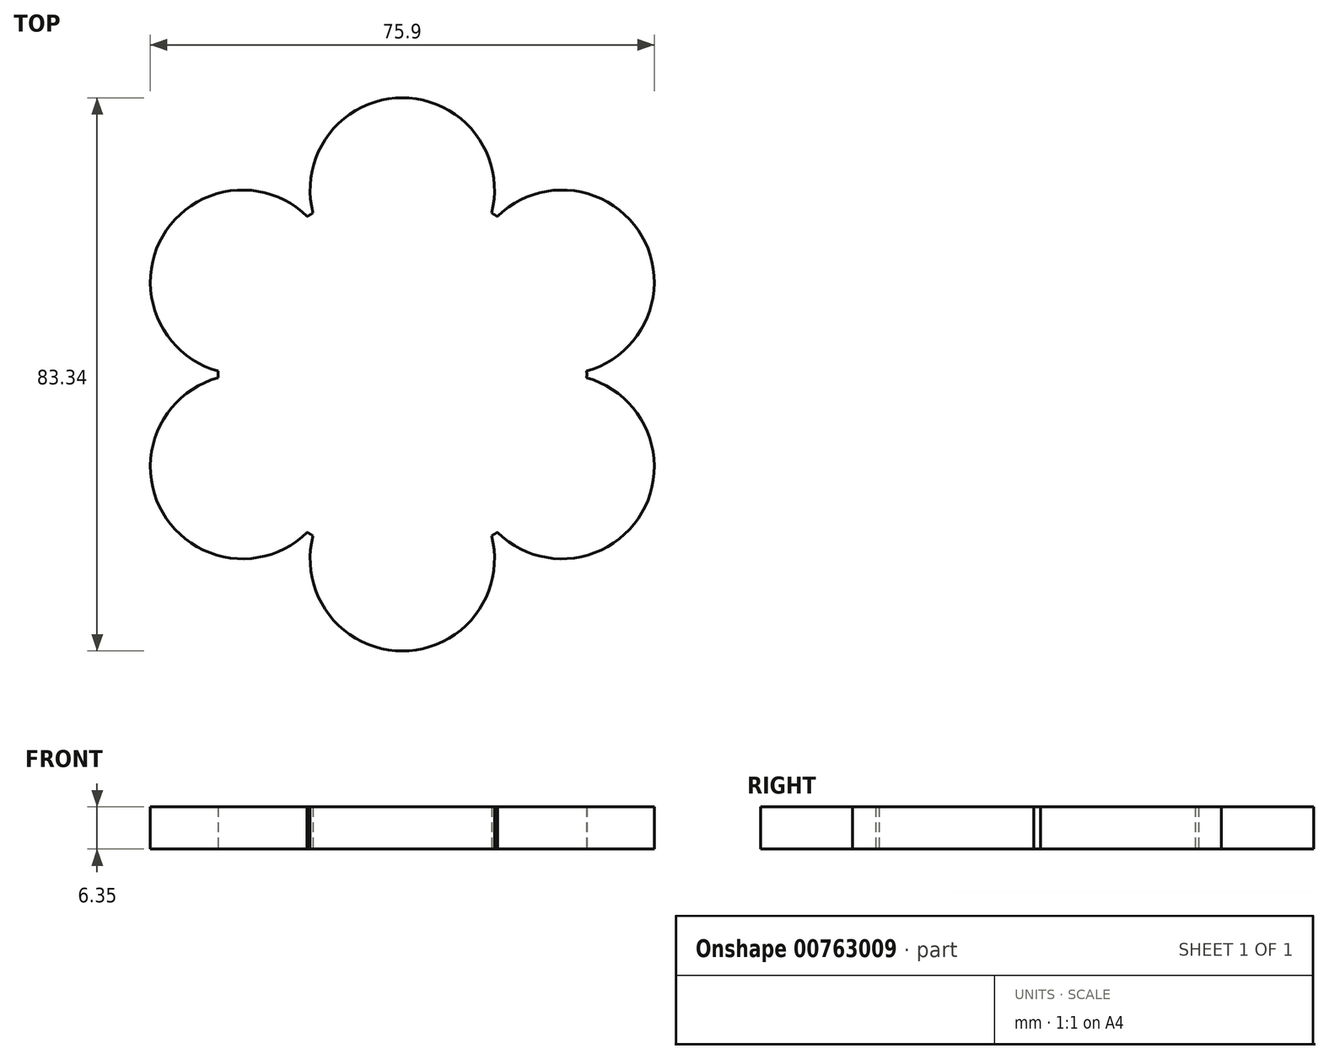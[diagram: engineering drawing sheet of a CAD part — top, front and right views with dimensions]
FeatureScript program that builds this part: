
annotation { "Feature Type Name" : "Feature", "Feature Type Description" : "" }
export const myFeature = defineFeature(function(context is Context, id is Id, definition is map)
    precondition{}
    {
        {
            var Q0;
            Q0=qCreatedBy(makeId("Top.planeOp"),FACE);
            var sketch = newSketch(context, id + "F0", { "sketchPlane" : qUnion([Q0])});
            skCircle(sketch, "E0", {"center": v(-24.06, 13.9) * mm, "radius": 13.9 * mm});
            skCircle(sketch, "E1", {"center": v(0, 27.78) * mm, "radius": 13.9 * mm});
            skPoint(sketch, "E1.centerSnap0", {"position": v(0, 24.75) * mm});
            skCircle(sketch, "E2", {"center": v(24.06, 13.9) * mm, "radius": 13.9 * mm});
            skCircle(sketch, "E3", {"center": v(0, -27.78) * mm, "radius": 13.9 * mm});
            skCircle(sketch, "E4", {"center": v(-24.06, -13.9) * mm, "radius": 13.9 * mm});
            skCircle(sketch, "E5", {"center": v(24.06, -13.9) * mm, "radius": 13.9 * mm});
            skCircle(sketch, "E6", {"center": v(0, 0) * mm, "radius": 27.78 * mm});
            skSolve(sketch);
        }
        {
            var Q0;
            Q0 = qSketchRegion(id + "F0", true);
            var Q1;
            {var subQ1=sQuery(id+"F0.wireOp",EDGE,"E1");var subQ5=sQuery(id+"F0.wireOp",EDGE,"E0");var subQ6=makeQuery(id+"F0.imprint","INTERSECT",VERTEX,{"derivedFrom":[subQ5,subQ1]});Q1=makeQuery(id+"F0.imprint","IMPRINT",FACE,{"disambiguationData":[TD([[makeQuery(id+"F0.imprint","IMPRINT",EDGE,{"disambiguationData":[TD([[subQ6,1.0]])],"derivedFrom":subQ5}),-1.0]])]});}
            extrude(context, id + "F1", {"entities" : qUnion([Q0, Q1]), "depth" : 25.4 * mm / 4, "offsetDistance" : 25.4 * mm});
        }
    });
